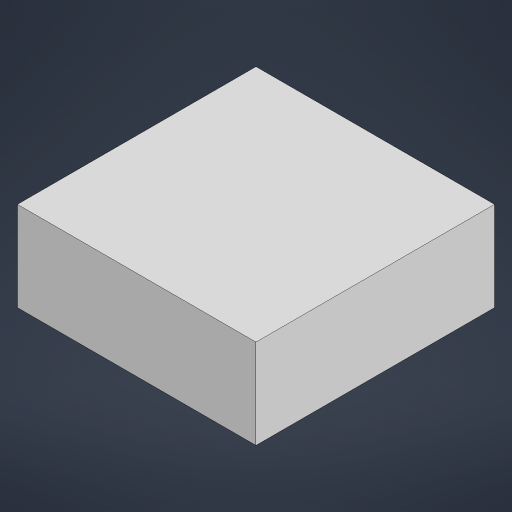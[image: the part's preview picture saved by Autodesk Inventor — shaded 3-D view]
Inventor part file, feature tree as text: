
AUTODESK INVENTOR PART (.ipt)
format: ipt  version: 2023.1 (Build 271208000, 208)  size: 135,168 bytes
history: native  units: in
note: dims shown in document units (in); Inventor stores cm internally (conversion verified against a paired STEP export)
features: extrude x1, sketch x1
ambient origin geometry x8: Origin, YZ Plane, XZ Plane, XY Plane, X Axis, Y Axis, Z Axis, Center Point
bodies: Solid1 (feature_tree)
feature tree (2):
  extrude  "Extrusion1"  Depth=8.0in
  sketch  "Sketch1"  dims[d0=8.0in d1=8.0in d2=3.0in d3=0.0in]
